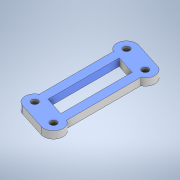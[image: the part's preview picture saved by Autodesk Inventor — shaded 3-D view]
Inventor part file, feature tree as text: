
AUTODESK INVENTOR PART (.ipt)
format: ipt  version: 2021 (Build 250183000, 183)  size: 179,200 bytes
history: native  units: mm
features: extrude x6, sketch x5, projected_geometry x1
ambient origin geometry x8: Origin, YZ Plane, XZ Plane, XY Plane, X Axis, Y Axis, Z Axis, Center Point
bodies: Solid1 (feature_tree)
feature tree (12):
  sketch  "Sketch1"  dims[d0=22.0mm d4=100.0mm]
  extrude  "Extrusion1"  Depth=100.0mm
  extrude  "Extrusion2"  Depth=9.0mm
  extrude  "Extrusion3"  Depth=6.0mm TaperAngle=0.0deg
  extrude  "Extrusion5"  Depth=2.9mm
  extrude  "Extrusion6"  Depth=10.0mm TaperAngle=0.0deg
  extrude  "Extrusion7"  Depth=10.0mm TaperAngle=0.0deg
  sketch  "Sketch2"  dims[d7=9.0mm d8=9.0mm]
  projected_geometry  "Projected Loop1"
  sketch  "Sketch4"  dims[d9=3.0mm d10=0.0mm d11=6.0mm d12=0.0mm]
  sketch  "Sketch5"  dims[d13=1.0mm d14=0.0mm d17=2.9mm]
  sketch  "Sketch6"  dims[d18=10.0mm d19=0.0mm d33=10.0mm d34=0.0mm d35=10.0mm d36=0.0mm]
